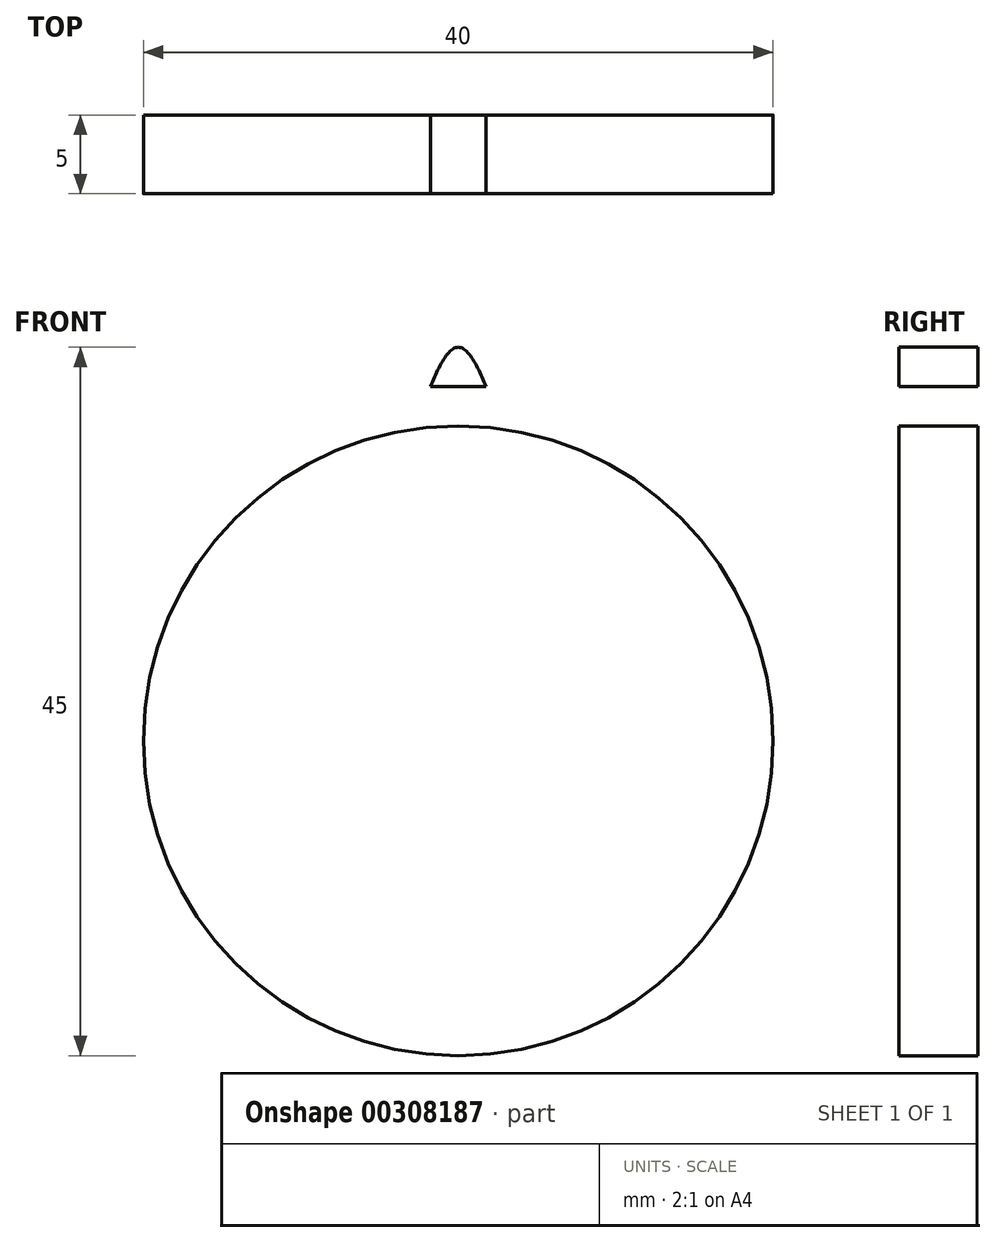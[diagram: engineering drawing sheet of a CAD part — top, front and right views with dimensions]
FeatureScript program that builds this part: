
annotation { "Feature Type Name" : "Feature", "Feature Type Description" : "" }
export const myFeature = defineFeature(function(context is Context, id is Id, definition is map)
    precondition{}
    {
        {
            var Q0;
            Q0=qCreatedBy(makeId("Front.planeOp"),FACE);
            var sketch = newSketch(context, id + "F0", { "sketchPlane" : qUnion([Q0])});
            skCircle(sketch, "E0", {"center": v(0, 0) * mm, "radius": 20 * mm});
            skLineSegment(sketch, "E1", {"start": v(0, 20) * mm, "end": v(2.5, 20) * mm, "construction": true});
            skLineSegment(sketch, "E2", {"start": v(2.5, 20) * mm, "end": v(2.5, 20) * mm});
            skLineSegment(sketch, "E3", {"start": v(0, 20) * mm, "end": v(-2.5, 20) * mm, "construction": true});
            skLineSegment(sketch, "E4", {"start": v(-2.5, 20) * mm, "end": v(-2.5, 19.84) * mm});
            skLineSegment(sketch, "E5", {"start": v(2.5, 20) * mm, "end": v(2.5, 19.84) * mm});
            skLineSegment(sketch, "E6", {"start": v(0, 20) * mm, "end": v(0, 25) * mm});
            skLineSegment(sketch, "E7", {"start": v(0, 20) * mm, "end": v(0, 22.5) * mm});
            skLineSegment(sketch, "E8", {"start": v(0, 22.5) * mm, "end": v(1.75, 22.5) * mm});
            skLineSegment(sketch, "E9", {"start": v(0, 22.5) * mm, "end": v(-1.75, 22.5) * mm});
            skFitSpline(sketch, "E10", {"points": [v(2.5, 19.84) * mm, v(1.75, 22.5) * mm, v(0, 25) * mm, v(-1.75, 22.5) * mm, v(-2.5, 19.84) * mm], "startDerivative": vector(-2.16, 9.86) * mm, "endDerivative": vector(-2.16, -9.86) * mm});
            skSolve(sketch);
        }
        {
            var Q0;
            {var subQ0=sQuery(id+"F0.wireOp",EDGE,"E10");var subQ1=sQuery(id+"F0.wireOp",EDGE,"E0");var subQ2=makeQuery(id+"F0.imprint","INTERSECT",VERTEX,{"disambiguationData":[OD(1.0)],"derivedFrom":[subQ1,subQ0]});Q0=makeQuery(id+"F0.imprint","IMPRINT",FACE,{"disambiguationData":[TD([[makeQuery(id+"F0.imprint","IMPRINT",EDGE,{"disambiguationData":[TD([[subQ2,-1.0]])],"derivedFrom":subQ1}),1.0]])]});}
            var Q1;
            {var subQ3=sQuery(id+"F0.wireOp",EDGE,"E7");Q1=makeQuery(id+"F0.imprint","IMPRINT",FACE,{"disambiguationData":[TD([[makeQuery(id+"F0.imprint","IMPRINT",EDGE,{"derivedFrom":subQ3}),-1.0]])]});}
            var Q2;
            {var subQ3=sQuery(id+"F0.wireOp",EDGE,"E7");Q2=makeQuery(id+"F0.imprint","IMPRINT",FACE,{"disambiguationData":[TD([[makeQuery(id+"F0.imprint","IMPRINT",EDGE,{"derivedFrom":subQ3}),1.0]])]});}
            var Q3;
            {var subQ0=sQuery(id+"F0.wireOp",EDGE,"E6");Q3=makeQuery(id+"F0.imprint","IMPRINT",FACE,{"disambiguationData":[TD([[makeQuery(id+"F0.imprint","IMPRINT",EDGE,{"derivedFrom":subQ0}),1.0]])]});}
            var Q4;
            {var subQ0=sQuery(id+"F0.wireOp",EDGE,"E6");Q4=makeQuery(id+"F0.imprint","IMPRINT",FACE,{"disambiguationData":[TD([[makeQuery(id+"F0.imprint","IMPRINT",EDGE,{"derivedFrom":subQ0}),-1.0]])]});}
            extrude(context, id + "F1", {"entities" : qUnion([Q0, Q1, Q2, Q3, Q4]), "depth" : 5 * mm});
        }
        {
            var Q0;
            Q0=makeQuery(id+"F1.opExtrude","SWEPT_BODY",BODY,{"disambiguationData":[OSD([sQuery(id+"F0.wireOp",EDGE,"E0"),sQuery(id+"F0.wireOp",EDGE,"E10")])]});
            var Q1;
            Q1=makeQuery(id+"F1.opExtrude","CAP_EDGE",EDGE,{"disambiguationData":[OSD([sQuery(id+"F0.wireOp",EDGE,"E0")])],"isStart":true});
            circularPattern(context, id + "F2", {"entities" : qUnion([Q0]), "axis" : qUnion([Q1]), "angle" : 360 * degree, "instanceCount" : 23, "equalSpace" : true});
        }
    });
